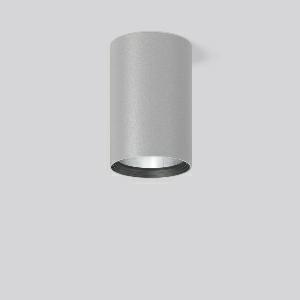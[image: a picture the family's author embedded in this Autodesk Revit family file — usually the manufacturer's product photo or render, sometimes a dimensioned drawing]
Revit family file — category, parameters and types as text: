
# Revit family: heledon_maxi_a_931223_004_914d
name_source: partatom
category: Lighting Fixtures
units: mm (PartAtom-declared; Revit-internal decimal feet)

## family parameters
Cut with Voids When Loaded = No
Host = Face
Light Source = No
Part Type = Normal
Room Calculation Point = No
Round Connector Dimension = Use Diameter
Shared = No

## types (1)
- HELEDON maxi A (1 x LED Modul 930, 4200 lm, 3000)
    Apparent Load = 35 VA
    Approval mark = CE
    CIE Flux Codes = 100 100 100 100 100
    Color Rendering = 90
    Color Temperature = 3000
    Default Elevation = 1800 mm
    Description = Series: HELEDON maxi
Cylindrical surface-mounted downlight. Housing: die-cast aluminium, powder-coated. Internal ceiling frame polycarbonate with bayonet mounting. Black plastic ring and recessed LED to prevent glare from the side. Optical assembly with reflector made of MIRO-Silver with 98% total light reflection for outstanding efficiency - can be changed without tools. Best colour rendering index Ra>90. Suitable for Ceiling mounting. Easy installation with a separate ceiling frame with bayonet mounting and plug connection. Driver integrated. Connected via plug-in connector. High quality converter without flickering and stroboscopic effect. The following accessories can be mounted without use of tools: interchangeable lenses, decorative glasses, honeycomb louvre, clear and frosted diffusers, white interchangeable plastic ring. 
Colour: silver
Diameter: 123 mm
Height: 183 mm
Lamp: LED
Socket: without socket
Colour temperature: 3000K
Colour rendering index (CRI): 92
System power: 35 W
Rated luminous flux: 4200 lm
Luminous efficiency: 120 lm/W
Control gear: Regulated power supply
Protection class: I
Type of protection: IP 20
    Height = 183 mm
    Lamp = 1 x LED Modul 930
    Lamp Light Flux = 4200 lm
    Lamp count = 1
    Length = 123 mm
    Lifetime = 50000 h
    Luminous efficacy = 120 lm/W
    Manufacturer = RZB
    ModVariant = No
    Model = 931223.004
    Mounting Place = Ceiling
    Mounting Type = Surface mounted
    Number of Poles = 1
    OnlyDefault = Yes
    Power Factor = 1
    Product Name = HELEDON maxi A
    Product group = Surface mounted downlights
    ProductGroupID = 302
    Protection Class = Protection class I
    Protection Degree = IP 20
    RLX_Detail_Level = 1
    RLX_Emergency_Light_Flux = 0 lm
    RLX_Emergency_Type = 0
    RLX_Emergency_Type_DB = No
    RlxData = <blob elided: 99409 chars, md5=1a468e99>
    Socket = socket
    Standby Power = 0 W
    System Light Flux = 4200 lm
    System Power = 35 W
    Type Comments = Product without accessories
    Type Image = 931192.004.jpg
    URL = http://relux.com
    VarID = ---
    Voltage = 230 V
    Voltage Range = 220-240 V
    Weight = 0.00 kg
    Width = 0 mm  [stored 0 ft]

note: [stored X ft] marks values corroborated as IEEE doubles in the binary element streams (Revit-internal decimal feet)

## geometry (parser evidence)
native form markers: Blend x4, Sweep x10
no freeform markers — native parametric forms only
